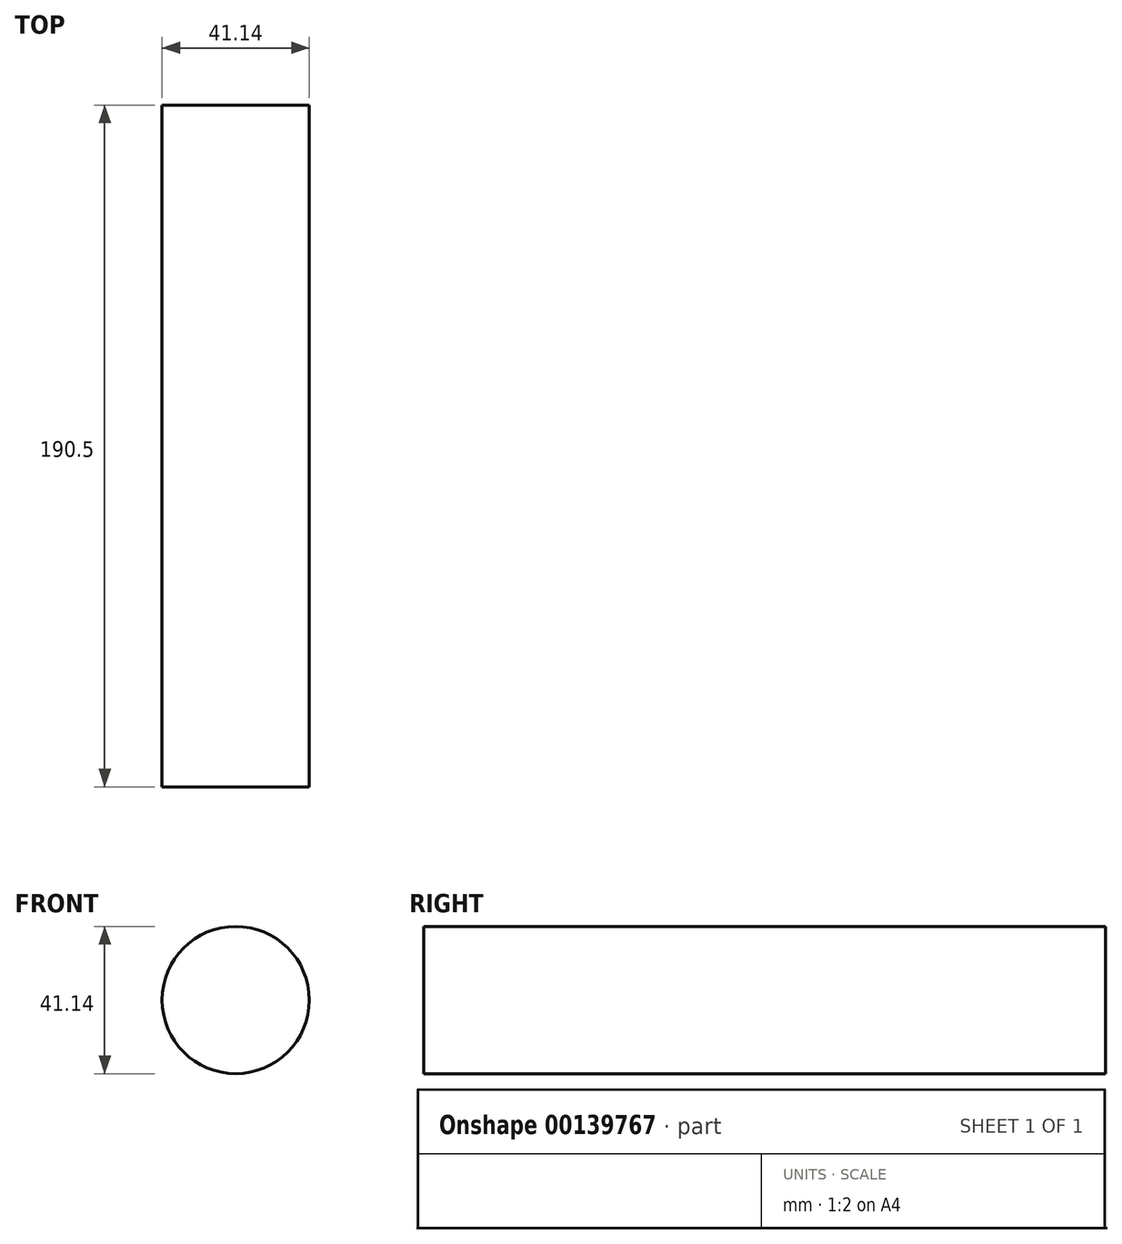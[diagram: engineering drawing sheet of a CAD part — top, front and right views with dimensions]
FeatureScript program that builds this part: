
annotation { "Feature Type Name" : "Feature", "Feature Type Description" : "" }
export const myFeature = defineFeature(function(context is Context, id is Id, definition is map)
    precondition{}
    {
        {
            var Q0;
            Q0=qCreatedBy(makeId("Front.planeOp"),FACE);
            var sketch = newSketch(context, id + "F0", { "sketchPlane" : qUnion([Q0])});
            skCircle(sketch, "E0", {"center": v(0, 0) * mm, "radius": 20.57 * mm});
            skSolve(sketch);
        }
        {
            var Q0;
            Q0 = qSketchRegion(id + "F0", true);
            extrude(context, id + "F1", {"entities" : qUnion([Q0]), "oppositeDirection" : true, "depth" : 190.5 * mm});
        }
    });
